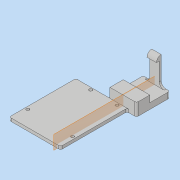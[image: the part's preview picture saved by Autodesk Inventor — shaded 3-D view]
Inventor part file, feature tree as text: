
AUTODESK INVENTOR PART (.ipt)
format: ipt  version: 2017 (Build 210142000, 142)  size: 179,200 bytes
history: native  units: in
note: dims shown in document units (in); Inventor stores cm internally (conversion verified against a paired STEP export)
features: extrude x5, sketch x5, fillet x2, plane x1
ambient origin geometry x8: Origin, YZ Plane, XZ Plane, XY Plane, X Axis, Y Axis, Z Axis, Center Point
bodies: Solid1 (feature_tree)
feature tree (13):
  extrude  "Extrusion1"  Depth=2.7559in
  extrude  "Extrusion2"  Depth=0.3937in
  extrude  "Extrusion3"  Depth=0.125in TaperAngle=0.0deg
  plane  "Work Plane1"
  extrude  "Extrusion4"  Depth=0.1181in TaperAngle=0.0deg
  extrude  "Extrusion5"  Depth=0.0787in
  fillet  "Fillet1"  Radius=1.1417in
  fillet  "Fillet2"  Radius=0.9449in
  sketch  "Sketch1"  dims[d0=2.126in d1=2.7559in]
  sketch  "Sketch2"  dims[d2=1.1024in d3=0.3937in]
  sketch  "Sketch3"  dims[d4=1.378in d5=0.125in d6=0.0in]
  sketch  "Sketch4"  dims[d7=0.5512in d8=0.1181in d9=0.0in]
  sketch  "Sketch5"  dims[d10=0.3937in d11=0.0in d12=0.0787in d13=1.1417in d14=0.9449in d15=0.1181in d16=0.3937in d17=0.0in d18=0.3937in d19=0.0in d20=0.0787in d21=0.0787in d22=0.1969in]
